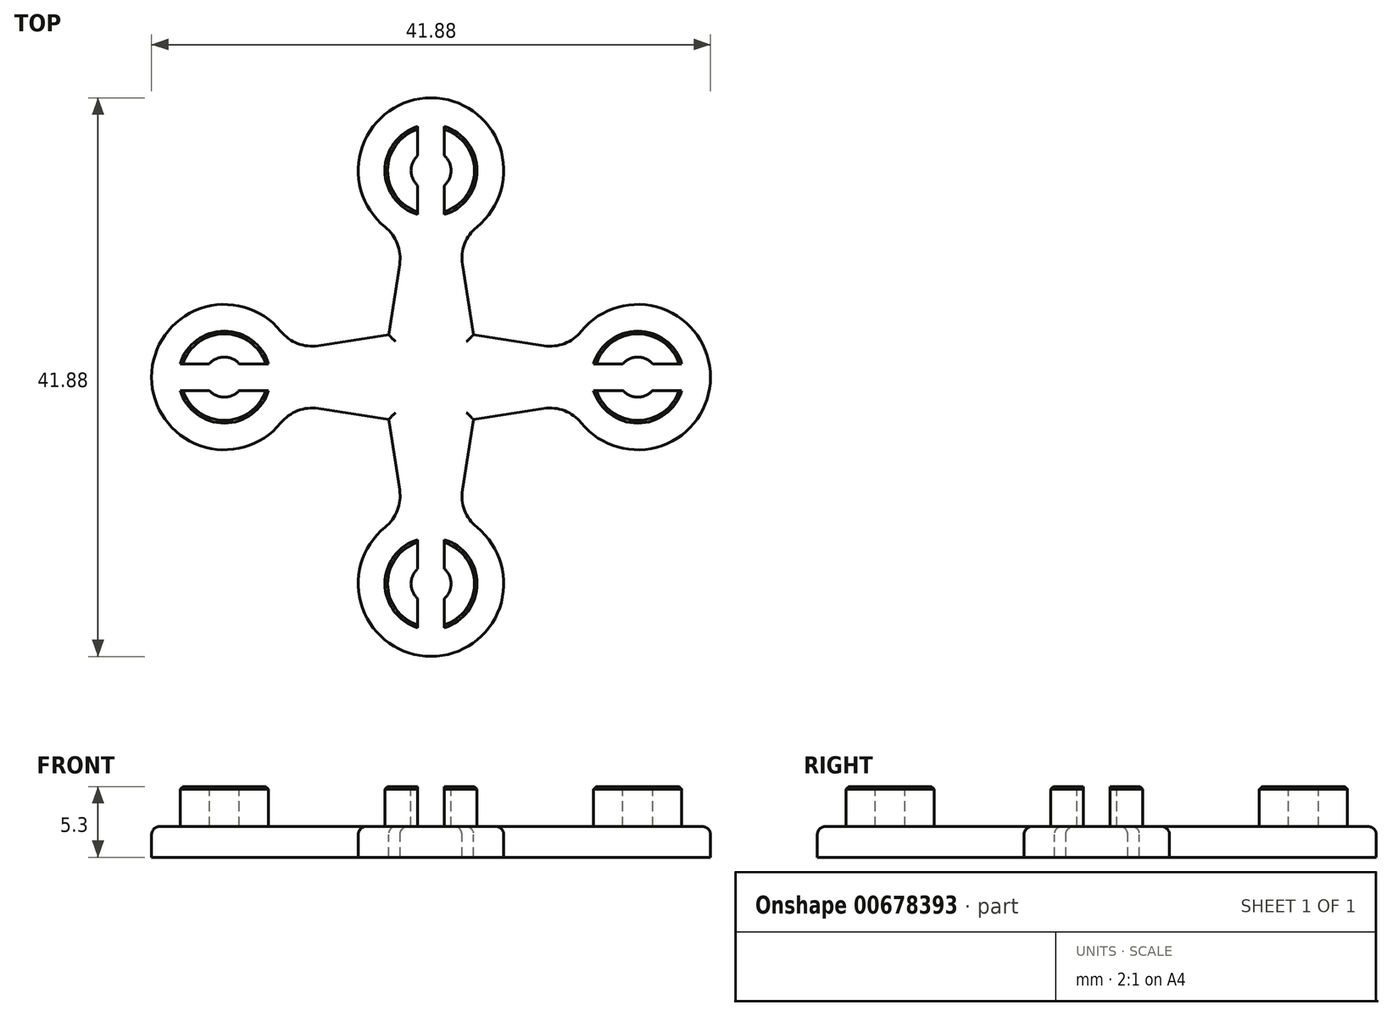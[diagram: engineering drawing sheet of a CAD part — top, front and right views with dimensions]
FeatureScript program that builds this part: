
annotation { "Feature Type Name" : "Feature", "Feature Type Description" : "" }
export const myFeature = defineFeature(function(context is Context, id is Id, definition is map)
    precondition{}
    {
        {
            var Q0;
            Q0=qCreatedBy(makeId("Top.planeOp"),FACE);
            var sketch = newSketch(context, id + "F0", { "sketchPlane" : qUnion([Q0])});
            skCircle(sketch, "E0", {"center": v(0, 15.49) * mm, "radius": 3.45 * mm});
            skPoint(sketch, "E1.center", {"position": v(0, 0) * mm});
            skSolve(sketch);
        }
        {
            var Q0;
            Q0 = qSketchRegion(id + "F0", true);
            extrude(context, id + "F1", {"entities" : qUnion([Q0]), "depth" : 3 * mm, "offsetDistance" : 25 * mm});
        }
        {
            var Q0;
            Q0=makeQuery(id+"F1.opExtrude","CAP_FACE",FACE,{"disambiguationData":[OSD([sQuery(id+"F0.wireOp",EDGE,"E0")])],"isStart":false});
            chamfer(context, id + "F2", {"entities" : qUnion([Q0]), "width" : 0.2 * mm, "tangentPropagation" : true});
        }
        {
            var Q0;
            Q0=makeQuery(id+"F1.opExtrude","CAP_FACE",FACE,{"disambiguationData":[OSD([sQuery(id+"F0.wireOp",EDGE,"E0")])],"isStart":false});
            var sketch = newSketch(context, id + "F3", { "sketchPlane" : qUnion([Q0])});
            skArc(sketch, "E2", {"start": v(-1, 16.6) * mm, "mid": v(-1.5, 15.49) * mm, "end": v(-1, 14.37) * mm});
            skLineSegment(sketch, "E3.bottom", {"start": v(1, 11.53) * mm, "end": v(-1, 11.53) * mm});
            skLineSegment(sketch, "E3.top", {"start": v(1, 19.44) * mm, "end": v(-1, 19.44) * mm});
            skLineSegment(sketch, "E3.left", {"start": v(1, 11.53) * mm, "end": v(1, 14.37) * mm});
            skLineSegment(sketch, "E3.right", {"start": v(-1, 11.53) * mm, "end": v(-1, 14.37) * mm});
            skLineSegment(sketch, "E4.trimOffspring", {"start": v(1, 16.6) * mm, "end": v(1, 19.44) * mm});
            skLineSegment(sketch, "E5.trimOffspring", {"start": v(-1, 16.6) * mm, "end": v(-1, 19.44) * mm});
            skArc(sketch, "E6.trimOffspring", {"start": v(1, 14.37) * mm, "mid": v(1.5, 15.49) * mm, "end": v(1, 16.6) * mm});
            skSolve(sketch);
        }
        {
            var Q0;
            Q0 = qSketchRegion(id + "F3", true);
            extrude(context, id + "F4", {"entities" : qUnion([Q0]), "operationType" : NewBodyOperationType.REMOVE, "endBound" : BoundingType.UP_TO_NEXT, "oppositeDirection" : true, "depth" : 2.25 * mm, "offsetDistance" : 25 * mm});
        }
        {
            var Q0;
            Q0=qCreatedBy(makeId("Right.planeOp"),FACE);
            var sketch = newSketch(context, id + "F5", { "sketchPlane" : qUnion([Q0])});
            skLineSegment(sketch, "E7", {"start": v(0, -15.08) * mm, "end": v(0, 17.76) * mm, "construction": true});
            skSolve(sketch);
        }
        {
            var Q0;
            Q0=makeQuery(id+"F1.opExtrude","SWEPT_BODY",BODY,{"disambiguationData":[OSD([sQuery(id+"F0.wireOp",EDGE,"E0")])]});
            var Q1;
            Q1=sQuery(id+"F5.wireOp",EDGE,"E7");
            circularPattern(context, id + "F6", {"entities" : qUnion([Q0]), "axis" : qUnion([Q1]), "angle" : 360 * degree, "instanceCount" : 4, "equalSpace" : true});
        }
        {
            var Q0;
            Q0=qCreatedBy(makeId("Top.planeOp"),FACE);
            var sketch = newSketch(context, id + "F7", { "sketchPlane" : qUnion([Q0])});
            skArc(sketch, "E8.0", {"start": v(3.43, 11.25) * mm, "mid": v(0, 20.94) * mm, "end": v(-3.43, 11.25) * mm});
            skCircle(sketch, "E9.cCircle", {"center": v(0, 0) * mm, "radius": 4.5 * mm, "construction": true});
            skLineSegment(sketch, "E9.0", {"start": v(0, 4.5) * mm, "end": v(3.18, 3.18) * mm});
            skLineSegment(sketch, "E9.1", {"start": v(3.18, 3.18) * mm, "end": v(4.5, 0) * mm});
            skLineSegment(sketch, "E9.2", {"start": v(4.5, 0) * mm, "end": v(3.18, -3.18) * mm});
            skLineSegment(sketch, "E9.3", {"start": v(3.18, -3.18) * mm, "end": v(0, -4.5) * mm});
            skLineSegment(sketch, "E9.4", {"start": v(0, -4.5) * mm, "end": v(-3.18, -3.18) * mm});
            skLineSegment(sketch, "E9.5", {"start": v(-3.18, -3.18) * mm, "end": v(-4.5, 0) * mm});
            skLineSegment(sketch, "E9.6", {"start": v(-4.5, 0) * mm, "end": v(-3.18, 3.18) * mm});
            skLineSegment(sketch, "E9.7", {"start": v(-3.18, 3.18) * mm, "end": v(0, 4.5) * mm});
            skLineSegment(sketch, "E10", {"start": v(-1.25, 15.49) * mm, "end": v(1.25, 15.49) * mm, "construction": true});
            skLineSegment(sketch, "E11", {"start": v(3.18, 3.18) * mm, "end": v(2.35, 8.45) * mm});
            skLineSegment(sketch, "E12", {"start": v(-3.18, 3.18) * mm, "end": v(-2.35, 8.45) * mm});
            skPoint(sketch, "E13.visualSharp", {"position": v(2.04, 10.43) * mm});
            skArc(sketch, "E13.filletArc", {"start": v(3.43, 11.25) * mm, "mid": v(2.52, 10) * mm, "end": v(2.35, 8.45) * mm});
            skPoint(sketch, "E14.visualSharp", {"position": v(-2.04, 10.43) * mm});
            skArc(sketch, "E14.filletArc", {"start": v(-2.35, 8.45) * mm, "mid": v(-2.52, 10) * mm, "end": v(-3.43, 11.25) * mm});
            skArc(sketch, "E15.1.0", {"start": v(-11.25, 3.43) * mm, "mid": v(-20.94, 0) * mm, "end": v(-11.25, -3.43) * mm});
            skArc(sketch, "E15.1.1", {"start": v(-11.25, 3.43) * mm, "mid": v(-10, 2.52) * mm, "end": v(-8.45, 2.35) * mm});
            skArc(sketch, "E15.1.2", {"start": v(-8.45, -2.35) * mm, "mid": v(-10, -2.52) * mm, "end": v(-11.25, -3.43) * mm});
            skLineSegment(sketch, "E15.1.3", {"start": v(-3.18, 3.18) * mm, "end": v(-8.45, 2.35) * mm});
            skLineSegment(sketch, "E15.1.4", {"start": v(-3.18, -3.18) * mm, "end": v(-8.45, -2.35) * mm});
            skArc(sketch, "E15.2.0", {"start": v(-3.43, -11.25) * mm, "mid": v(0, -20.94) * mm, "end": v(3.43, -11.25) * mm});
            skArc(sketch, "E15.2.1", {"start": v(-3.43, -11.25) * mm, "mid": v(-2.52, -10) * mm, "end": v(-2.35, -8.45) * mm});
            skArc(sketch, "E15.2.2", {"start": v(2.35, -8.45) * mm, "mid": v(2.52, -10) * mm, "end": v(3.43, -11.25) * mm});
            skLineSegment(sketch, "E15.2.3", {"start": v(-3.18, -3.18) * mm, "end": v(-2.35, -8.45) * mm});
            skLineSegment(sketch, "E15.2.4", {"start": v(3.18, -3.18) * mm, "end": v(2.35, -8.45) * mm});
            skArc(sketch, "E15.3.0", {"start": v(11.25, -3.43) * mm, "mid": v(20.94, 0) * mm, "end": v(11.25, 3.43) * mm});
            skArc(sketch, "E15.3.1", {"start": v(11.25, -3.43) * mm, "mid": v(10, -2.52) * mm, "end": v(8.45, -2.35) * mm});
            skArc(sketch, "E15.3.2", {"start": v(8.45, 2.35) * mm, "mid": v(10, 2.52) * mm, "end": v(11.25, 3.43) * mm});
            skLineSegment(sketch, "E15.3.3", {"start": v(3.18, -3.18) * mm, "end": v(8.45, -2.35) * mm});
            skLineSegment(sketch, "E15.3.4", {"start": v(3.18, 3.18) * mm, "end": v(8.45, 2.35) * mm});
            skSolve(sketch);
        }
        {
            var Q0;
            Q0 = qSketchRegion(id + "F7", true);
            var Q1;
            Q1=makeQuery(id+"F7.imprint","IMPRINT",FACE,{"disambiguationData":[TD([[makeQuery(id+"F7.imprint","IMPRINT",EDGE,{"derivedFrom":sQuery(id+"F7.wireOp",EDGE,"1d5718fb-3d77-4ac8-90fd-aeaac3141486.0")}),-1.0]])]});
            extrude(context, id + "F8", {"entities" : qUnion([Q0, Q1]), "oppositeDirection" : true, "depth" : 2.3 * mm, "offsetDistance" : 25 * mm});
        }
        {
            var Q0;
            Q0=makeQuery(id+"F8.opExtrude","CAP_FACE",FACE,{"disambiguationData":[OSD([sQuery(id+"F7.wireOp",EDGE,"E8.0"),sQuery(id+"F7.wireOp",EDGE,"E11"),sQuery(id+"F7.wireOp",EDGE,"E12"),sQuery(id+"F7.wireOp",EDGE,"E13.filletArc"),sQuery(id+"F7.wireOp",EDGE,"E14.filletArc"),sQuery(id+"F7.wireOp",EDGE,"E15.1.0"),sQuery(id+"F7.wireOp",EDGE,"E15.1.1"),sQuery(id+"F7.wireOp",EDGE,"E15.1.2"),sQuery(id+"F7.wireOp",EDGE,"E15.1.3"),sQuery(id+"F7.wireOp",EDGE,"E15.1.4"),sQuery(id+"F7.wireOp",EDGE,"E15.2.0"),sQuery(id+"F7.wireOp",EDGE,"E15.2.1"),sQuery(id+"F7.wireOp",EDGE,"E15.2.2"),sQuery(id+"F7.wireOp",EDGE,"E15.2.3"),sQuery(id+"F7.wireOp",EDGE,"E15.2.4"),sQuery(id+"F7.wireOp",EDGE,"E15.3.0"),sQuery(id+"F7.wireOp",EDGE,"E15.3.1"),sQuery(id+"F7.wireOp",EDGE,"E15.3.2"),sQuery(id+"F7.wireOp",EDGE,"E15.3.3"),sQuery(id+"F7.wireOp",EDGE,"E15.3.4")])],"isStart":true});
            fillet(context, id + "F9", {"entities" : qUnion([Q0]), "radius" : 0.6 * mm, "tangentPropagation" : true, "allowEdgeOverflow" : false});
        }
    });
